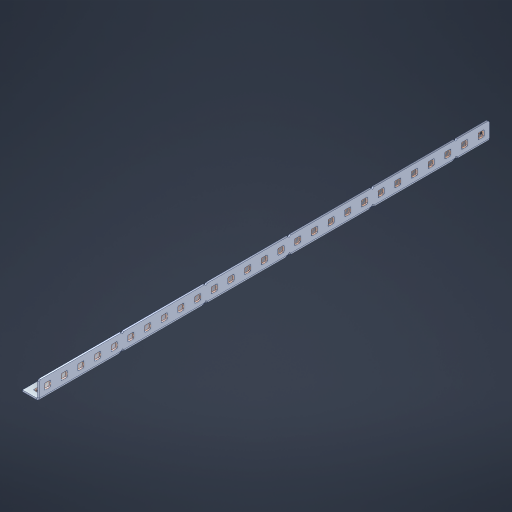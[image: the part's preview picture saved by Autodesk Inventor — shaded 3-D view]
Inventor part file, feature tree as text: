
AUTODESK INVENTOR PART (.ipt)
format: ipt  version: 2023 (Build 270158000, 158)  size: 891,392 bytes
history: native  units: in
note: dims shown in document units (in); Inventor stores cm internally (conversion verified against a paired STEP export)
features: other x59, extrude x53, sheet_metal_op x10, sketch x8, mirror x1, pattern_linear x1, chamfer x1
ambient origin geometry x8: Origin, YZ Plane, XZ Plane, XY Plane, X Axis, Y Axis, Z Axis, Center Point
bodies: Solid1 (feature_tree), Body (feature_tree)
feature tree (133):
  other  "Flange Pattern Plane"
  sheet_metal_op  "Flange Pattern"
  sheet_metal_op  "Body Pattern"
  other  "Arc Length"
  mirror  "Notch Mirror"
  pattern_linear  "Notch Pattern"  Spacing1=0.1875in  [1 undecoded]
  chamfer  "End Chamfer"
  extrude  "Half Cut"  Depth=0.0469in
  sketch  "Sketch1"  dims[d0=2.5in]
  other  "Plate1"
  sketch  "Sketch2"  dims[d1=13.5in]
  other  "Plate2"
  sheet_metal_op  "Bend1"
  sheet_metal_op  "Corner1"
  sketch  "Sketch3"  dims[d2=0.0469in]
  other  "Flange Pattern Sketch"
  sketch  "Sketch7"  dims[d3=0.0469in]
  other  "Srf1"
  other  "Srf2"
  sketch  "Sketch8"  dims[d4=0.0234in]
  sketch  "Sketch9"  dims[d5=0.0938in]
  other  "Srf91"
  sheet_metal_op  "Body Pattern Sketch"
  other  "Srf92"
  sketch  "Sketch13"  dims[d6=0.0469in]
  sketch  "Sketch14"  dims[d7=0.5in d8=90.0deg d9=0.0312in d10=0.1875in d11=0.0469in d12=0.0469in d16=0.182in d17=0.02in d18=0.0469in d19=0.0in d20=0.25in d21=0.25in d46=0.172in d47=1.0in d48=0.0in d49=0.182in d50=0.02in d51=0.25in d52=0.25in d53=0.0469in d54=0.0in d55=0.172in d56=1.0in d57=0.0in d60=10.6299in d62=0.5in d63=0.3937in d65=0.5in d85=0.1227in d86=0.1659in d88=0.04in d89=0.0469in d90=0.0in d91=0.04in d92=0.0491in d95=2.5in d96=0.04in d97=0.25in d98=45.0deg d101=0.0in d102=2.497in d131=0.5in d132=10.6299in d134=0.5in d139=0.5in]
  other  "Srf856"
  other  "Srf1310"
  other  "Srf1311"
  other  "Srf1312"
  other  "Srf1376"
  other  "Srf1377"
  other  "Srf1728"
  other  "Srf1755"
  other  "Srf1878"
  other  "Srf1879"
  other  "Srf1880"
  other  "Srf1881"
  other  "Srf1882"
  other  "Srf1883"
  other  "Srf1884"
  other  "Srf1885"
  other  "Srf1886"
  other  "Srf1887"
  other  "Srf1888"
  other  "Srf1889"
  other  "Srf1890"
  other  "Srf1891"
  other  "Srf1892"
  other  "Srf1893"
  other  "Srf1894"
  other  "Srf1895"
  other  "Srf1896"
  other  "Srf1897"
  other  "Srf1898"
  other  "Srf1942"
  other  "Srf1943"
  other  "Srf1944"
  other  "Srf1945"
  other  "Srf1946"
  other  "Srf1947"
  other  "Srf1948"
  other  "Srf1949"
  other  "Srf1950"
  other  "Srf1951"
  other  "Srf1952"
  other  "Srf1953"
  other  "Srf1954"
  other  "Srf1955"
  other  "Srf1956"
  other  "Srf1957"
  other  "Srf1958"
  other  "Srf1959"
  other  "Srf1960"
  other  "Srf1961"
  other  "Srf1962"
  sheet_metal_op  "Flange Stamp"
  sheet_metal_op  "Flange Circle"
  sheet_metal_op  "Body Stamp"
  sheet_metal_op  "Body Circle"
  sheet_metal_op  "Notch"
  extrude  "ExtrusionSrf2"  Depth=0.0469in
  extrude  "ExtrusionSrf92"  Depth=0.5in
  extrude  "ExtrusionSrf856"  Depth=0.02in
  extrude  "ExtrusionSrf1310"  Depth=0.0469in
  extrude  "ExtrusionSrf1311"  TaperAngle=0.0deg  [1 undecoded]
  extrude  "ExtrusionSrf1312"  Depth=0.5in
  extrude  "ExtrusionSrf1376"  Depth=0.5in
  extrude  "ExtrusionSrf1377"  Depth=0.5in
  extrude  "ExtrusionSrf1728"  Depth=0.5in TaperAngle=0.0deg
  extrude  "ExtrusionSrf1755"  Depth=0.5in
  extrude  "ExtrusionSrf1878"  Depth=0.02in
  extrude  "ExtrusionSrf1879"  Depth=0.5in
  extrude  "ExtrusionSrf1880"  Depth=0.5in
  extrude  "ExtrusionSrf1881"  Depth=0.0469in
  extrude  "ExtrusionSrf1882"  TaperAngle=0.0deg  [1 undecoded]
  extrude  "ExtrusionSrf1883"  Depth=0.5in
  extrude  "ExtrusionSrf1884"  Depth=0.5in TaperAngle=0.0deg
  extrude  "ExtrusionSrf1885"  Depth=0.5in
  extrude  "ExtrusionSrf1886"  Depth=0.5in
  extrude  "ExtrusionSrf1887"  Depth=0.5in
  extrude  "ExtrusionSrf1888"  Depth=0.5in
  extrude  "ExtrusionSrf1889"  Depth=0.5in
  extrude  "ExtrusionSrf1890"  Depth=0.0469in
  extrude  "ExtrusionSrf1891"  TaperAngle=0.0deg  [1 undecoded]
  extrude  "ExtrusionSrf1892"  Depth=0.5in
  extrude  "ExtrusionSrf1893"  Depth=0.5in
  extrude  "ExtrusionSrf1894"  Depth=0.5in
  extrude  "ExtrusionSrf1895"  Depth=0.5in TaperAngle=45.0deg
  extrude  "ExtrusionSrf1896"  TaperAngle=0.0deg  [1 undecoded]
  extrude  "ExtrusionSrf1897"  Depth=0.5in
  extrude  "ExtrusionSrf1898"  Depth=0.5in
  extrude  "ExtrusionSrf1942"  Depth=0.5in
  extrude  "ExtrusionSrf1943"  Depth=0.5in
  extrude  "ExtrusionSrf1944"  Depth=0.5in
  extrude  "ExtrusionSrf1945"  [1 undecoded]
  extrude  "ExtrusionSrf1946"  [1 undecoded]
  extrude  "ExtrusionSrf1947"  [1 undecoded]
  extrude  "ExtrusionSrf1948"  [1 undecoded]
  extrude  "ExtrusionSrf1949"  [1 undecoded]
  extrude  "ExtrusionSrf1950"  [1 undecoded]
  extrude  "ExtrusionSrf1951"  [1 undecoded]
  extrude  "ExtrusionSrf1952"  [1 undecoded]
  extrude  "ExtrusionSrf1953"  [1 undecoded]
  extrude  "ExtrusionSrf1954"  [1 undecoded]
  extrude  "ExtrusionSrf1955"  [1 undecoded]
  extrude  "ExtrusionSrf1956"  [1 undecoded]
  extrude  "ExtrusionSrf1957"  [1 undecoded]
  extrude  "ExtrusionSrf1958"  [1 undecoded]
  extrude  "ExtrusionSrf1959"  [1 undecoded]
  extrude  "ExtrusionSrf1960"  [1 undecoded]
  extrude  "ExtrusionSrf1961"  [1 undecoded]
  extrude  "ExtrusionSrf1962"  [1 undecoded]
note: 23 required parameter values undecoded (feature->parameter linkage not recoverable at this tier; creation-order binding heuristic only, values carry confidence <= 0.55)
